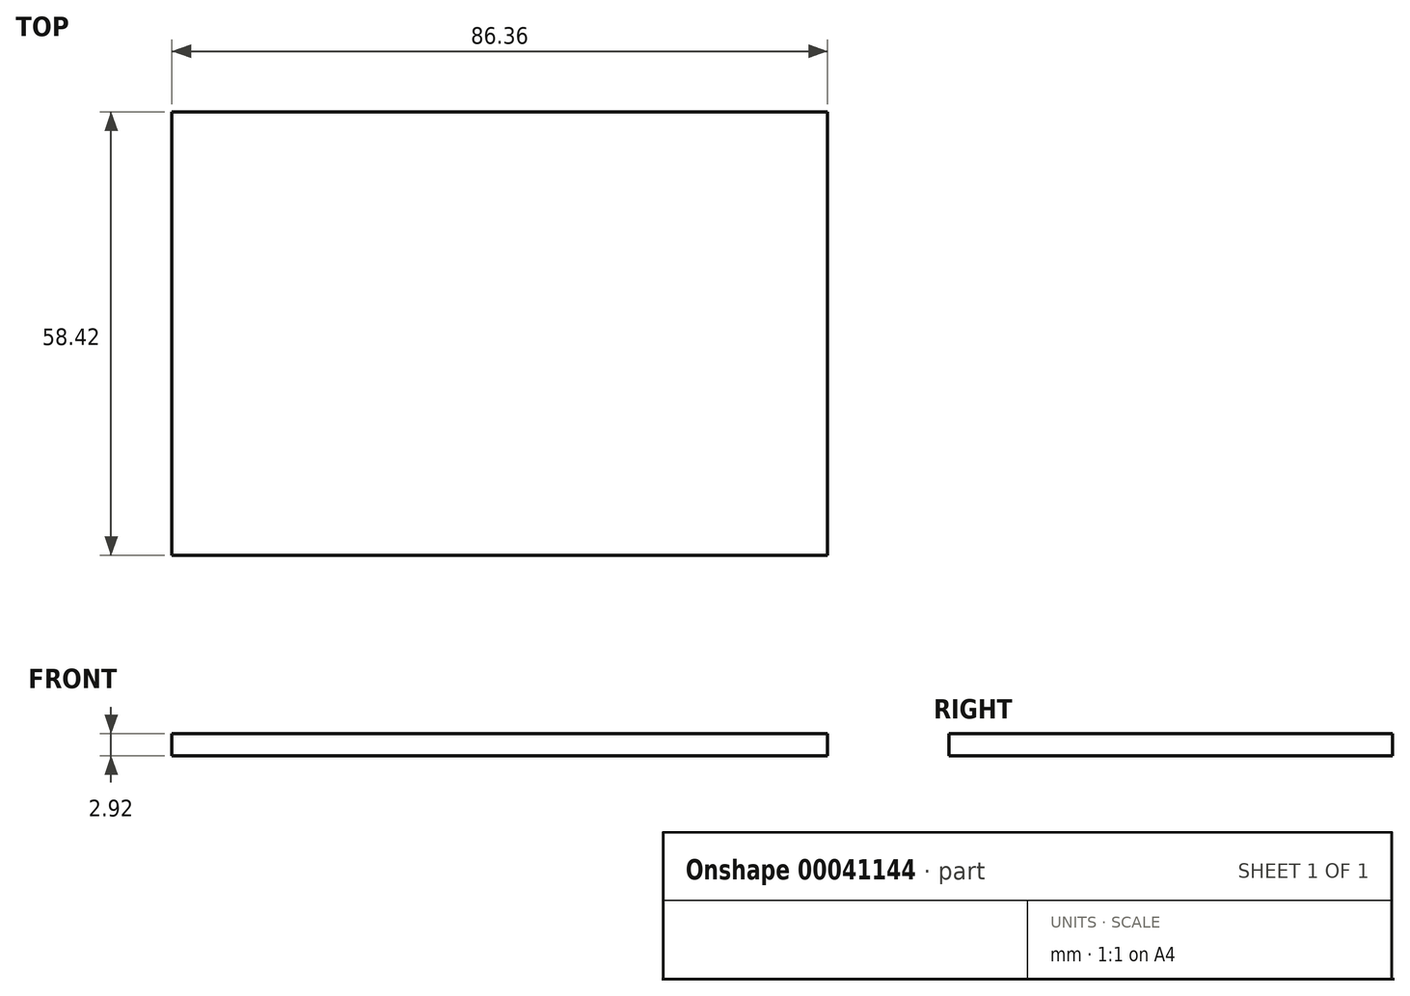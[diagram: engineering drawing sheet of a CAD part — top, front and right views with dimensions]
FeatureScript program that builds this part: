
annotation { "Feature Type Name" : "Feature", "Feature Type Description" : "" }
export const myFeature = defineFeature(function(context is Context, id is Id, definition is map)
    precondition{}
    {
        {
            var Q0;
            Q0=qCreatedBy(makeId("Top.planeOp"),FACE);
            var sketch = newSketch(context, id + "F0", { "sketchPlane" : qUnion([Q0])});
            skLineSegment(sketch, "E0.bottom", {"start": v(9.7, 26.4) * mm, "end": v(-76.65, 26.4) * mm});
            skLineSegment(sketch, "E0.top", {"start": v(9.7, -32.02) * mm, "end": v(-76.65, -32.02) * mm});
            skLineSegment(sketch, "E0.left", {"start": v(9.7, 26.4) * mm, "end": v(9.7, -32.02) * mm});
            skLineSegment(sketch, "E0.right", {"start": v(-76.65, 26.4) * mm, "end": v(-76.65, -32.02) * mm});
            skSolve(sketch);
        }
        {
            var Q0;
            Q0=makeQuery(id+"F0.imprint","IMPRINT",FACE,{"disambiguationData":[TD([[makeQuery(id+"F0.imprint","IMPRINT",EDGE,{"derivedFrom":sQuery(id+"F0.wireOp",EDGE,"E0.bottom")}),1.0]])]});
            extrude(context, id + "F1", {"entities" : qUnion([Q0]), "oppositeDirection" : true, "depth" : 2.92 * mm});
        }
    });
